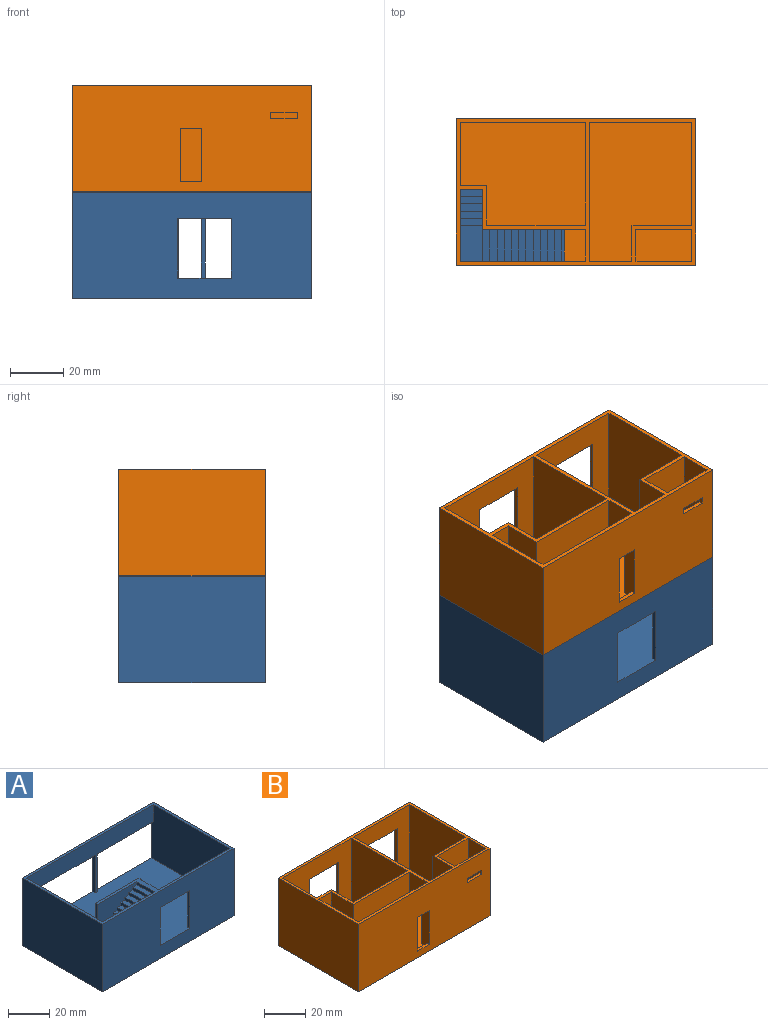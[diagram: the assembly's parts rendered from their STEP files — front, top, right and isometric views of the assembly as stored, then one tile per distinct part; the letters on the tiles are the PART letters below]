
ASSEMBLY  parts=2 mates=1
PART A: 68 faces, bbox 90x55x40 mm
  f0: plane 90x40mm, normal (0,-1,0), area 3150mm2, adj f11,f12,f13,f14,f19,f65,f66,f67
  f1: plane 1.2x0.76mm, normal (1,0,0), area 0.5mm2, adj f5,f28,f64
  f2: plane 35.5x18.7mm, normal (0,1,0), area 411.4mm2, adj f6,f8,f13,f26,f43,f44,f45,f46
  f3: plane 87x32.3mm, normal (0,1,0), area 1858.5mm2, adj f13,f15,f16,f19,f27,f63,f64,f65
  f4: plane 27x17mm, normal (0,-1,0), area 252.5mm2, adj f6,f13,f43,f44,f45,f46,f47,f48
  f5: plane 32.3x30mm, normal (0,-1,0), area 640.8mm2, adj f1,f7,f13,f18,f19,f63,f64
  f6: plane 18.7x13.5mm, normal (-1,0,0), area 48.5mm2, adj f2,f4,f13,f17,f26,f43
  f7: plane 11.14x1.5mm, normal (-1,0,0), area 16mm2, adj f5,f17,f19,f28
  f8: plane 52x32.3mm, normal (1,0,0), area 1367.5mm2, adj f2,f10,f13,f17,f19,f26,f29,f30
  f9: plane 90x40mm, normal (0,1,0), area 1882.9mm2, adj f11,f12,f13,f14,f16,f19,f20,f21
  f10: plane 87x32.3mm, normal (0,-1,0), area 1093mm2, adj f8,f13,f16,f19,f20,f21,f22,f23
  f11: plane 55x40mm, normal (-1,0,0), area 2200mm2, adj f0,f9,f13,f14
  f12: plane 55x40mm, normal (1,0,0), area 2200mm2, adj f0,f9,f13,f14
  f13: plane 90x55mm, normal (0,0,1), area 503.4mm2, adj f0,f2,f3,f4,f5,f6,f8,f9
  f14: plane 90x55mm, normal (0,0,-1), area 4950mm2, adj f0,f9,f11,f12
  f15: plane 29.7x11.9mm, normal (1,0,0), area 241mm2, adj f3,f19,f27,f28
  f16: plane 53.5x32.3mm, normal (-1,0,0), area 1713mm2, adj f3,f9,f10,f13,f19,f23
  f17: plane 38.5x32.3mm, normal (0,1,0), area 983.5mm2, adj f6,f7,f8,f13,f18,f19,f25,f26
  f18: plane 32.3x1.5mm, normal (1,0,0), area 48.4mm2, adj f5,f13,f17,f19
  f19: plane 87x55mm, normal (0,0,1), area 4601.6mm2, adj f0,f3,f5,f7,f8,f9,f10,f15
  f20: plane 22.3x1.5mm, normal (-1,0,0), area 33.5mm2, adj f9,f10,f19,f21
  f21: plane 38.5x1.5mm, normal (0,0,-1), area 57.8mm2, adj f9,f10,f20,f22
  f22: plane 22.3x1.5mm, normal (1,0,0), area 33.5mm2, adj f9,f10,f19,f21
  f23: plane 38.5x1.5mm, normal (0,0,-1), area 57.8mm2, adj f9,f10,f16,f24
  f24: plane 22.3x1.5mm, normal (1,0,0), area 33.5mm2, adj f9,f10,f19,f23
  f25: plane 18.9x11.9mm, normal (1,0,0), area 45.9mm2, adj f17,f19,f28,f29,f30,f31,f32,f33
  f26: plane 13.5x8.5mm, normal (0,0,1), area 114.8mm2, adj f2,f6,f8,f17
  f27: plane 10.8x8.5mm, normal (0,0,-1), area 91.8mm2, adj f3,f15,f28,f64
  f28: plane 18.9x11.9mm, normal (0,-0.53,-0.85), area 189.8mm2, adj f1,f7,f15,f19,f25,f27
  f29: plane 8.5x1.7mm, normal (0,1,0), area 14.5mm2, adj f8,f19,f25,f30
  f30: plane 8.5x2.7mm, normal (0,0,1), area 23mm2, adj f8,f25,f29,f31
  f31: plane 8.5x1.7mm, normal (0,1,0), area 14.5mm2, adj f8,f25,f30,f32
  f32: plane 8.5x2.7mm, normal (0,0,1), area 22.9mm2, adj f8,f25,f31,f33
  f33: plane 8.5x1.7mm, normal (0,1,0), area 14.5mm2, adj f8,f25,f32,f34
  f34: plane 8.5x2.7mm, normal (0,0,1), area 23mm2, adj f8,f25,f33,f35
  f35: plane 8.5x1.7mm, normal (0,1,0), area 14.5mm2, adj f8,f25,f34,f36
  f36: plane 8.5x2.7mm, normal (0,0,1), area 23mm2, adj f8,f25,f35,f37
  f37: plane 8.5x1.7mm, normal (0,1,0), area 14.4mm2, adj f8,f25,f36,f38
  f38: plane 8.5x2.7mm, normal (0,0,1), area 22.9mm2, adj f8,f25,f37,f39
  f39: plane 8.5x1.7mm, normal (0,1,0), area 14.5mm2, adj f8,f25,f38,f40
  f40: plane 8.5x2.7mm, normal (0,0,1), area 23mm2, adj f8,f25,f39,f41
  f41: plane 8.5x1.7mm, normal (0,1,0), area 14.5mm2, adj f8,f25,f40,f42
  f42: plane 8.5x2.7mm, normal (0,0,1), area 23mm2, adj f8,f17,f25,f41
  f43: plane 12x2.7mm, normal (0,0,1), area 32.4mm2, adj f2,f4,f6,f44
  f44: plane 12x1.7mm, normal (-1,0,0), area 20.4mm2, adj f2,f4,f43,f45
  f45: plane 12x2.7mm, normal (0,0,1), area 32.4mm2, adj f2,f4,f44,f46
  f46: plane 12x1.7mm, normal (-1,0,0), area 20.4mm2, adj f2,f4,f45,f47
  f47: plane 12x2.7mm, normal (0,0,1), area 32.4mm2, adj f2,f4,f46,f48
  f48: plane 12x1.7mm, normal (-1,0,0), area 20.4mm2, adj f2,f4,f47,f49
  f49: plane 12x2.7mm, normal (0,0,1), area 32.4mm2, adj f2,f4,f48,f50
  f50: plane 12x1.7mm, normal (-1,0,0), area 20.4mm2, adj f2,f4,f49,f51
  f51: plane 12x2.7mm, normal (0,0,1), area 32.4mm2, adj f2,f4,f50,f52
  f52: plane 12x1.7mm, normal (-1,0,0), area 20.4mm2, adj f2,f4,f51,f53
  f53: plane 12x2.7mm, normal (0,0,1), area 32.4mm2, adj f2,f4,f52,f54
  f54: plane 12x1.7mm, normal (-1,0,0), area 20.4mm2, adj f2,f4,f53,f55
  f55: plane 12x2.7mm, normal (0,0,1), area 32.4mm2, adj f2,f4,f54,f56
  f56: plane 12x1.7mm, normal (-1,0,0), area 20.4mm2, adj f2,f4,f55,f57
  f57: plane 12x2.7mm, normal (0,0,1), area 32.4mm2, adj f2,f4,f56,f58
  f58: plane 12x1.7mm, normal (-1,0,0), area 20.4mm2, adj f2,f4,f57,f59
  f59: plane 12x2.7mm, normal (0,0,1), area 32.4mm2, adj f2,f4,f58,f60
  f60: plane 12x1.7mm, normal (-1,0,0), area 20.4mm2, adj f2,f4,f59,f61
  f61: plane 12x2.7mm, normal (0,0,1), area 32.4mm2, adj f2,f4,f60,f62
  f62: plane 12x1.7mm, normal (-1,0,0), area 20.4mm2, adj f2,f4,f13,f61
  f63: plane 12x1.7mm, normal (1,0,0), area 20.4mm2, adj f3,f5,f13,f64
  f64: plane 29.7x18.7mm, normal (0.53,0,-0.85), area 421.2mm2, adj f1,f3,f5,f27,f63
  f65: plane 22.5x1.5mm, normal (-1,0,0), area 33.8mm2, adj f0,f3,f19,f67
  f66: plane 22.5x1.5mm, normal (1,0,0), area 33.8mm2, adj f0,f3,f19,f67
  f67: plane 20x1.5mm, normal (0,0,-1), area 30mm2, adj f0,f3,f65,f66
PART B: 52 faces, bbox 90x55x40 mm
  f0: plane 90x40mm, normal (0,-1,0), area 3415mm2, adj f7,f11,f12,f13,f14,f45,f46,f47
  f1: plane 38.5x21mm, normal (0,1,0), area 783.5mm2, adj f10,f11,f23,f29,f45,f46,f47,f48
  f2: plane 90x40mm, normal (0,1,0), area 2720mm2, adj f11,f12,f13,f14,f37,f38,f39,f40
  f3: plane 38.5x38.5mm, normal (0,-1,0), area 1042.2mm2, adj f8,f11,f16,f29,f41,f42,f43,f44
  f4: plane 47x38.5mm, normal (0,-1,0), area 1369.5mm2, adj f11,f25,f26,f29,f37,f38,f39,f40
  f5: plane 40x38.5mm, normal (0,-1,0), area 1348mm2, adj f7,f11,f14,f19,f34,f35,f36
  f6: plane 38.5x37mm, normal (0,1,0), area 1244.5mm2, adj f11,f25,f28,f29,f34,f35
  f7: plane 38.5x13.5mm, normal (-1,0,0), area 312mm2, adj f0,f5,f11,f22,f29,f32,f33,f49
  f8: plane 52x38.5mm, normal (1,0,0), area 1822mm2, adj f3,f11,f17,f18,f29,f32,f33
  f9: plane 38.5x13.5mm, normal (-1,0,0), area 339.7mm2, adj f11,f15,f17,f24,f29,f30,f31
  f10: plane 38.5x12mm, normal (1,0,0), area 282mm2, adj f1,f11,f24,f29,f30,f31
  f11: plane 90x55mm, normal (0,0,1), area 648.8mm2, adj f0,f1,f2,f3,f4,f5,f6,f7
  f12: plane 55x40mm, normal (-1,0,0), area 2200mm2, adj f0,f2,f11,f14
  f13: plane 55x40mm, normal (1,0,0), area 2200mm2, adj f0,f2,f11,f14
  f14: plane 90x55mm, normal (0,0,-1), area 4354.5mm2, adj f0,f2,f5,f12,f13,f19,f20,f21
  f15: plane 38.5x22.5mm, normal (0,1,0), area 866.2mm2, adj f9,f11,f16,f29
  f16: plane 38.5x38.5mm, normal (-1,0,0), area 1482.2mm2, adj f3,f11,f15,f29
  f17: plane 38.5x16mm, normal (0,1,0), area 616mm2, adj f8,f9,f11,f29
  f18: plane 22.5x1.5mm, normal (0,-1,0), area 33.8mm2, adj f8,f25,f29,f32
  f19: plane 40x15mm, normal (-1,0,0), area 600mm2, adj f5,f11,f14,f20
  f20: plane 40x8.5mm, normal (0,-1,0), area 340mm2, adj f11,f14,f19,f21
  f21: plane 40x27mm, normal (1,0,0), area 1080mm2, adj f11,f14,f20,f22
  f22: plane 47x40mm, normal (0,1,0), area 1708mm2, adj f7,f11,f14,f21,f29,f36,f49,f50
  f23: plane 38.5x12mm, normal (-1,0,0), area 462mm2, adj f1,f11,f24,f29
  f24: plane 38.5x22.5mm, normal (0,-1,0), area 842.2mm2, adj f9,f10,f11,f23,f29,f31
  f25: plane 40x38.5mm, normal (-1,0,0), area 1516mm2, adj f4,f6,f11,f18,f29,f34
  f26: plane 38.5x23.5mm, normal (1,0,0), area 904.7mm2, adj f4,f11,f27,f29
  f27: plane 38.5x10mm, normal (0,1,0), area 385mm2, adj f11,f26,f28,f29
  f28: plane 38.5x15mm, normal (1,0,0), area 577.5mm2, adj f6,f11,f27,f29
  f29: plane 87x52mm, normal (0,0,1), area 3741.7mm2, adj f1,f3,f4,f6,f7,f8,f9,f10
  f30: plane 22.5x1.5mm, normal (0,1,0), area 33.8mm2, adj f9,f10,f29,f31
  f31: plane 8x1.5mm, normal (0,0,-1), area 12mm2, adj f9,f10,f24,f30
  f32: plane 8x1.5mm, normal (0,0,-1), area 12mm2, adj f7,f8,f18,f33
  f33: plane 22.5x1.5mm, normal (0,1,0), area 33.8mm2, adj f7,f8,f29,f32
  f34: plane 8x1.5mm, normal (0,0,-1), area 12mm2, adj f5,f6,f25,f35
  f35: plane 22.5x1.5mm, normal (1,0,0), area 33.7mm2, adj f5,f6,f29,f34
  f36: plane 12x1.5mm, normal (-1,0,0), area 18mm2, adj f5,f14,f22,f29
  f37: plane 20x1.5mm, normal (0,0,-1), area 30mm2, adj f2,f4,f38,f40
  f38: plane 22x1.5mm, normal (-1,0,0), area 33mm2, adj f2,f4,f37,f39
  f39: plane 20x1.5mm, normal (0,0,1), area 30mm2, adj f2,f4,f38,f40
  f40: plane 22x1.5mm, normal (1,0,0), area 33mm2, adj f2,f4,f37,f39
  f41: plane 20x1.5mm, normal (0,0,-1), area 30mm2, adj f2,f3,f42,f44
  f42: plane 22x1.5mm, normal (-1,0,0), area 33mm2, adj f2,f3,f41,f43
  f43: plane 20x1.5mm, normal (0,0,1), area 30mm2, adj f2,f3,f42,f44
  f44: plane 22x1.5mm, normal (1,0,0), area 33mm2, adj f2,f3,f41,f43
  f45: plane 10x1.5mm, normal (0,0,-1), area 15mm2, adj f0,f1,f46,f48
  f46: plane 2.5x1.5mm, normal (1,0,0), area 3.7mm2, adj f0,f1,f45,f47
  f47: plane 10x1.5mm, normal (0,0,1), area 15mm2, adj f0,f1,f46,f48
  f48: plane 2.5x1.5mm, normal (-1,0,0), area 3.7mm2, adj f0,f1,f45,f47
  f49: plane 8x1.5mm, normal (0,0,-1), area 12mm2, adj f0,f7,f22,f51
  f50: plane 8x1.5mm, normal (0,0,1), area 12mm2, adj f0,f7,f22,f51
  f51: plane 20x1.5mm, normal (1,0,0), area 30mm2, adj f0,f22,f49,f50
PLACE A t=(-14.3,-1.54,-0.15)mm
PLACE B t=(-14.3,-1.54,39.85)mm
MATE fastened B.f13 <-> A.f12  axis (1,0,0) through (75.7,-1.54,39.85)mm
